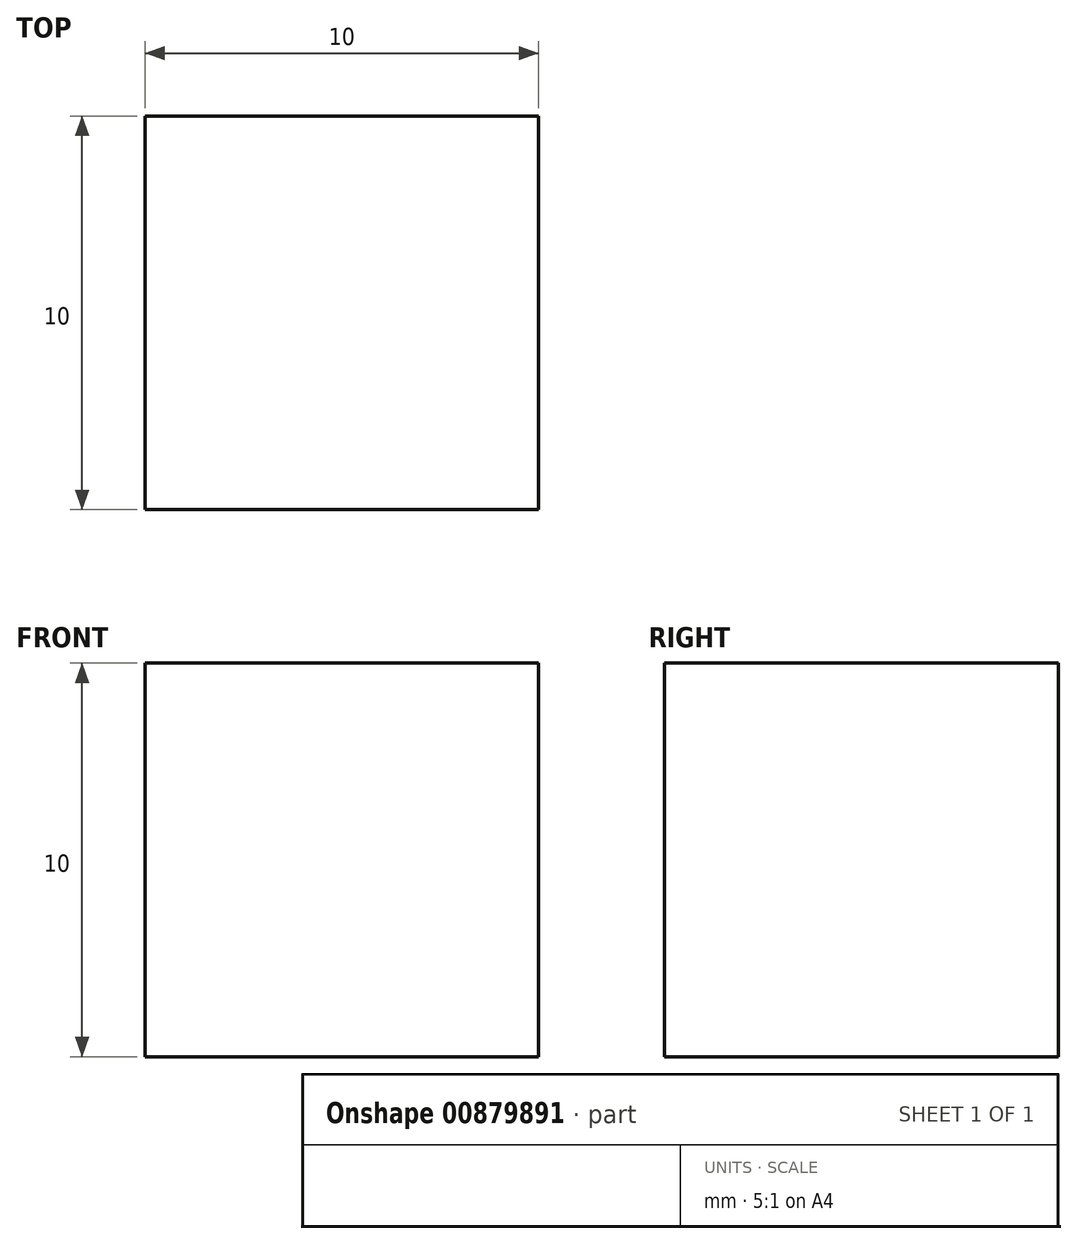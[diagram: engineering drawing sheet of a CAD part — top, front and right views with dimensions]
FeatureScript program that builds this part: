
annotation { "Feature Type Name" : "Feature", "Feature Type Description" : "" }
export const myFeature = defineFeature(function(context is Context, id is Id, definition is map)
    precondition{}
    {
        {
            var Q0;
            Q0=qCreatedBy(makeId("Top.planeOp"),FACE);
            var sketch = newSketch(context, id + "F0", { "sketchPlane" : qUnion([Q0])});
            skLineSegment(sketch, "E0.bottom", {"start": v(5, 5) * mm, "end": v(-5, 5) * mm});
            skLineSegment(sketch, "E0.top", {"start": v(5, -5) * mm, "end": v(-5, -5) * mm});
            skLineSegment(sketch, "E0.left", {"start": v(5, 5) * mm, "end": v(5, -5) * mm});
            skLineSegment(sketch, "E0.right", {"start": v(-5, 5) * mm, "end": v(-5, -5) * mm});
            skPoint(sketch, "E0.middle", {"position": v(0, 0) * mm});
            skLineSegment(sketch, "E1", {"start": v(0, 0) * mm, "end": v(5, 0) * mm, "construction": true});
            skSolve(sketch);
        }
        {
            var Q0;
            Q0 = qSketchRegion(id + "F0", true);
            extrude(context, id + "F1", {"entities" : qUnion([Q0]), "depth" : 10 * mm, "offsetDistance" : 25 * mm});
        }
    });
